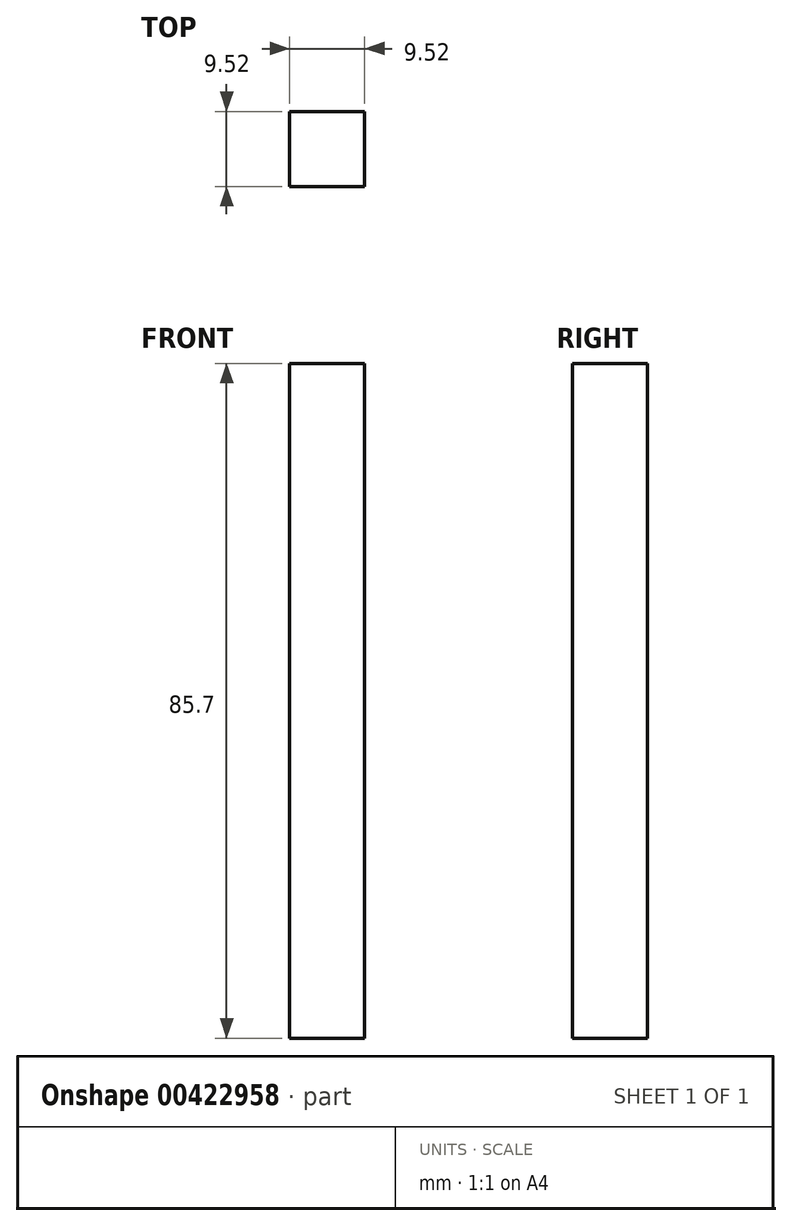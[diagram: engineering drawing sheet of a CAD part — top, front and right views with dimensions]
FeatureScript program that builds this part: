
annotation { "Feature Type Name" : "Feature", "Feature Type Description" : "" }
export const myFeature = defineFeature(function(context is Context, id is Id, definition is map)
    precondition{}
    {
        {
            var Q0;
            Q0=qCreatedBy(makeId("Top.planeOp"),FACE);
            var sketch = newSketch(context, id + "F0", { "sketchPlane" : qUnion([Q0])});
            skPoint(sketch, "E0.middle", {"position": v(0, 0) * mm});
            skLineSegment(sketch, "E1.bottom", {"start": v(4.76, 4.76) * mm, "end": v(-4.76, 4.76) * mm});
            skLineSegment(sketch, "E1.top", {"start": v(4.76, -4.76) * mm, "end": v(-4.76, -4.76) * mm});
            skLineSegment(sketch, "E1.left", {"start": v(4.76, 4.76) * mm, "end": v(4.76, -4.76) * mm});
            skLineSegment(sketch, "E1.right", {"start": v(-4.76, 4.76) * mm, "end": v(-4.76, -4.76) * mm});
            skSolve(sketch);
        }
        {
            var Q0;
            Q0 = qSketchRegion(id + "F0", true);
            extrude(context, id + "F1", {"entities" : qUnion([Q0]), "depth" : 85.7 * mm, "offsetDistance" : 25.4 * mm});
        }
    });
